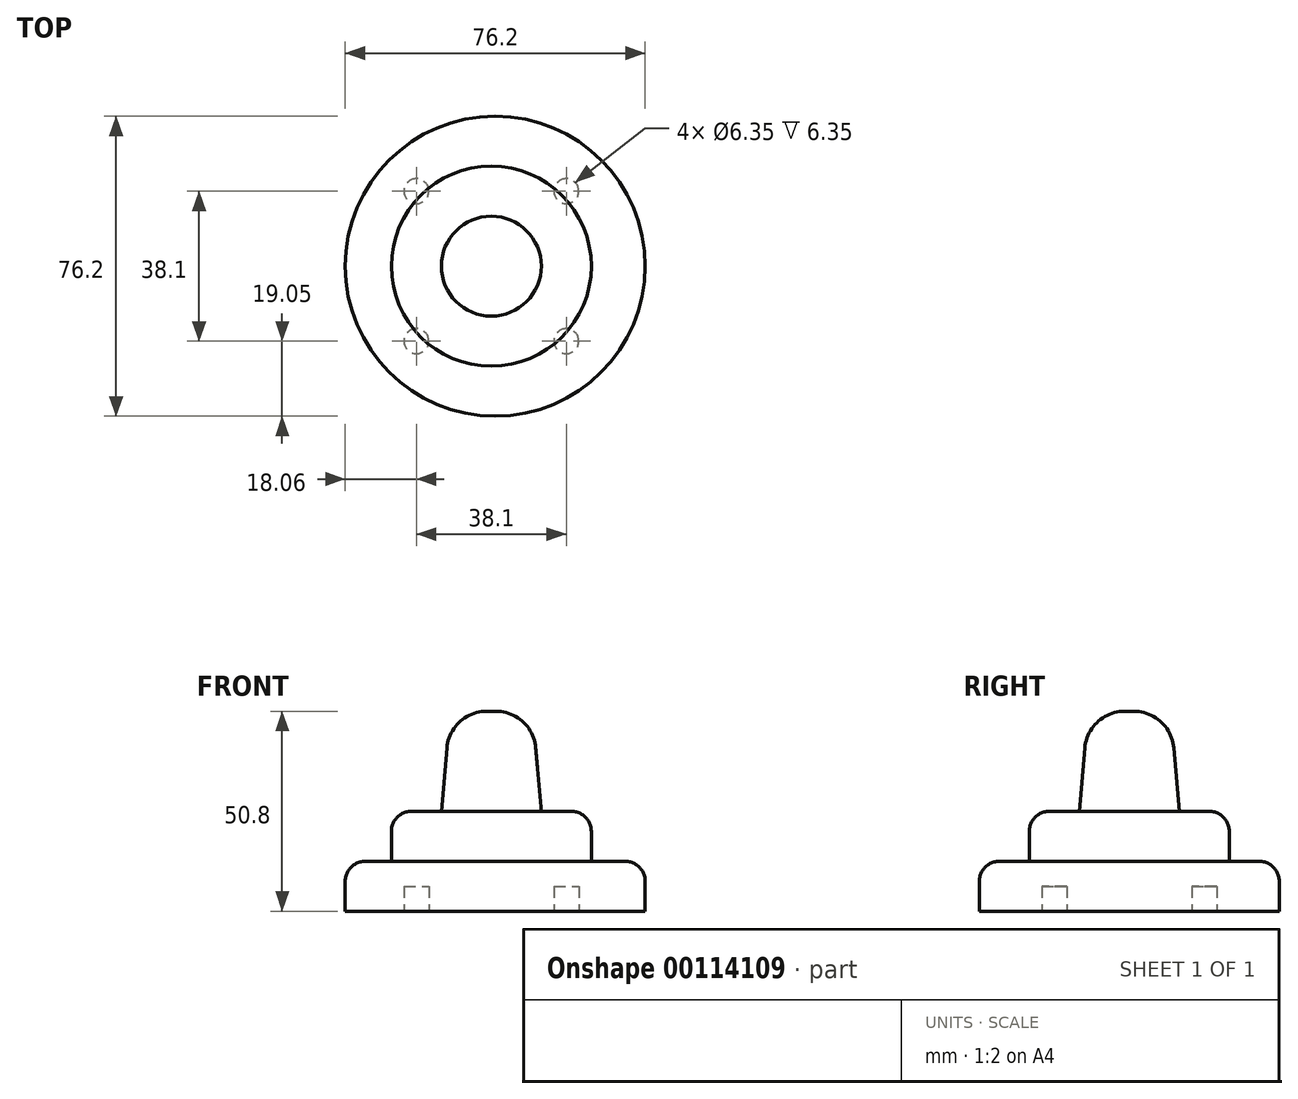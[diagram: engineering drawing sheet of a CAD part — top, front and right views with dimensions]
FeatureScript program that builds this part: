
annotation { "Feature Type Name" : "Feature", "Feature Type Description" : "" }
export const myFeature = defineFeature(function(context is Context, id is Id, definition is map)
    precondition{}
    {
        {
            var Q0;
            Q0=qCreatedBy(makeId("Top.planeOp"),FACE);
            var sketch = newSketch(context, id + "F0", { "sketchPlane" : qUnion([Q0])});
            skCircle(sketch, "E0", {"center": v(0.99, 0) * mm, "radius": 38.1 * mm});
            skSolve(sketch);
        }
        {
            var Q0;
            Q0 = qSketchRegion(id + "F0", true);
            extrude(context, id + "F1", {"entities" : qUnion([Q0]), "depth" : 12.7 * mm});
        }
        {
            var Q0;
            Q0=makeQuery(id+"F1.opExtrude","CAP_FACE",FACE,{"disambiguationData":[OSD([sQuery(id+"F0.wireOp",EDGE,"E0")])],"isStart":true});
            var sketch = newSketch(context, id + "F2", { "sketchPlane" : qUnion([Q0])});
            skCircle(sketch, "E1", {"center": v(-19.05, -19.05) * mm, "radius": 3.18 * mm});
            skCircle(sketch, "E2.1.0", {"center": v(19.05, -19.05) * mm, "radius": 3.18 * mm});
            skCircle(sketch, "E2.2.0", {"center": v(19.05, 19.05) * mm, "radius": 3.18 * mm});
            skCircle(sketch, "E2.3.0", {"center": v(-19.05, 19.05) * mm, "radius": 3.18 * mm});
            skPoint(sketch, "E2.center", {"position": v(0, 0) * mm});
            skSolve(sketch);
        }
        {
            var Q0;
            Q0 = qSketchRegion(id + "F2", true);
            extrude(context, id + "F3", {"entities" : qUnion([Q0]), "operationType" : NewBodyOperationType.REMOVE, "oppositeDirection" : true, "depth" : 6.35 * mm});
        }
        {
            var Q0;
            Q0=makeQuery(id+"F1.opExtrude","CAP_FACE",FACE,{"disambiguationData":[OSD([sQuery(id+"F0.wireOp",EDGE,"E0")])],"isStart":false});
            var sketch = newSketch(context, id + "F4", { "sketchPlane" : qUnion([Q0])});
            skCircle(sketch, "E3", {"center": v(0, 0) * mm, "radius": 25.4 * mm});
            skSolve(sketch);
        }
        {
            var Q0;
            Q0 = qSketchRegion(id + "F4", true);
            extrude(context, id + "F5", {"entities" : qUnion([Q0]), "operationType" : NewBodyOperationType.ADD, "depth" : 12.7 * mm});
        }
        {
            var Q0;
            Q0=makeQuery(id+"F5.opExtrude","CAP_FACE",FACE,{"disambiguationData":[OSD([sQuery(id+"F4.wireOp",EDGE,"E3")])],"isStart":false});
            var sketch = newSketch(context, id + "F6", { "sketchPlane" : qUnion([Q0])});
            skCircle(sketch, "E4", {"center": v(0, 0) * mm, "radius": 12.7 * mm});
            skSolve(sketch);
        }
        {
            var Q0;
            Q0 = qSketchRegion(id + "F6", true);
            extrude(context, id + "F7", {"entities" : qUnion([Q0]), "operationType" : NewBodyOperationType.ADD, "depth" : 25.4 * mm, "hasDraft" : true, "draftAngle" : 5 * degree, "draftPullDirection" : true});
        }
        {
            var Q0;
            Q0=makeQuery(id+"F1.opExtrude","CAP_EDGE",EDGE,{"disambiguationData":[OSD([sQuery(id+"F0.wireOp",EDGE,"E0")])],"isStart":false});
            var Q1;
            Q1=makeQuery(id+"F5.opExtrude","CAP_EDGE",EDGE,{"disambiguationData":[OSD([sQuery(id+"F4.wireOp",EDGE,"E3")])],"isStart":true});
            var Q2;
            Q2=makeQuery(id+"F5.opExtrude","CAP_EDGE",EDGE,{"disambiguationData":[OSD([sQuery(id+"F4.wireOp",EDGE,"E3")])],"isStart":false});
            var Q3;
            Q3=makeQuery(id+"F7.opExtrude","CAP_EDGE",EDGE,{"disambiguationData":[OSD([sQuery(id+"F6.wireOp",EDGE,"E4")])],"isStart":true});
            fillet(context, id + "F8", {"entities" : qUnion([Q0, Q1, Q2, Q3]), "radius" : 5.08 * mm, "tangentPropagation" : true, "allowEdgeOverflow" : false});
        }
        {
            var Q0;
            Q0=makeQuery(id+"F7.opExtrude","CAP_EDGE",EDGE,{"disambiguationData":[OSD([sQuery(id+"F6.wireOp",EDGE,"E4")])],"isStart":false});
            fillet(context, id + "F9", {"entities" : qUnion([Q0]), "radius" : 10.16 * mm, "tangentPropagation" : true, "allowEdgeOverflow" : false});
        }
    });
